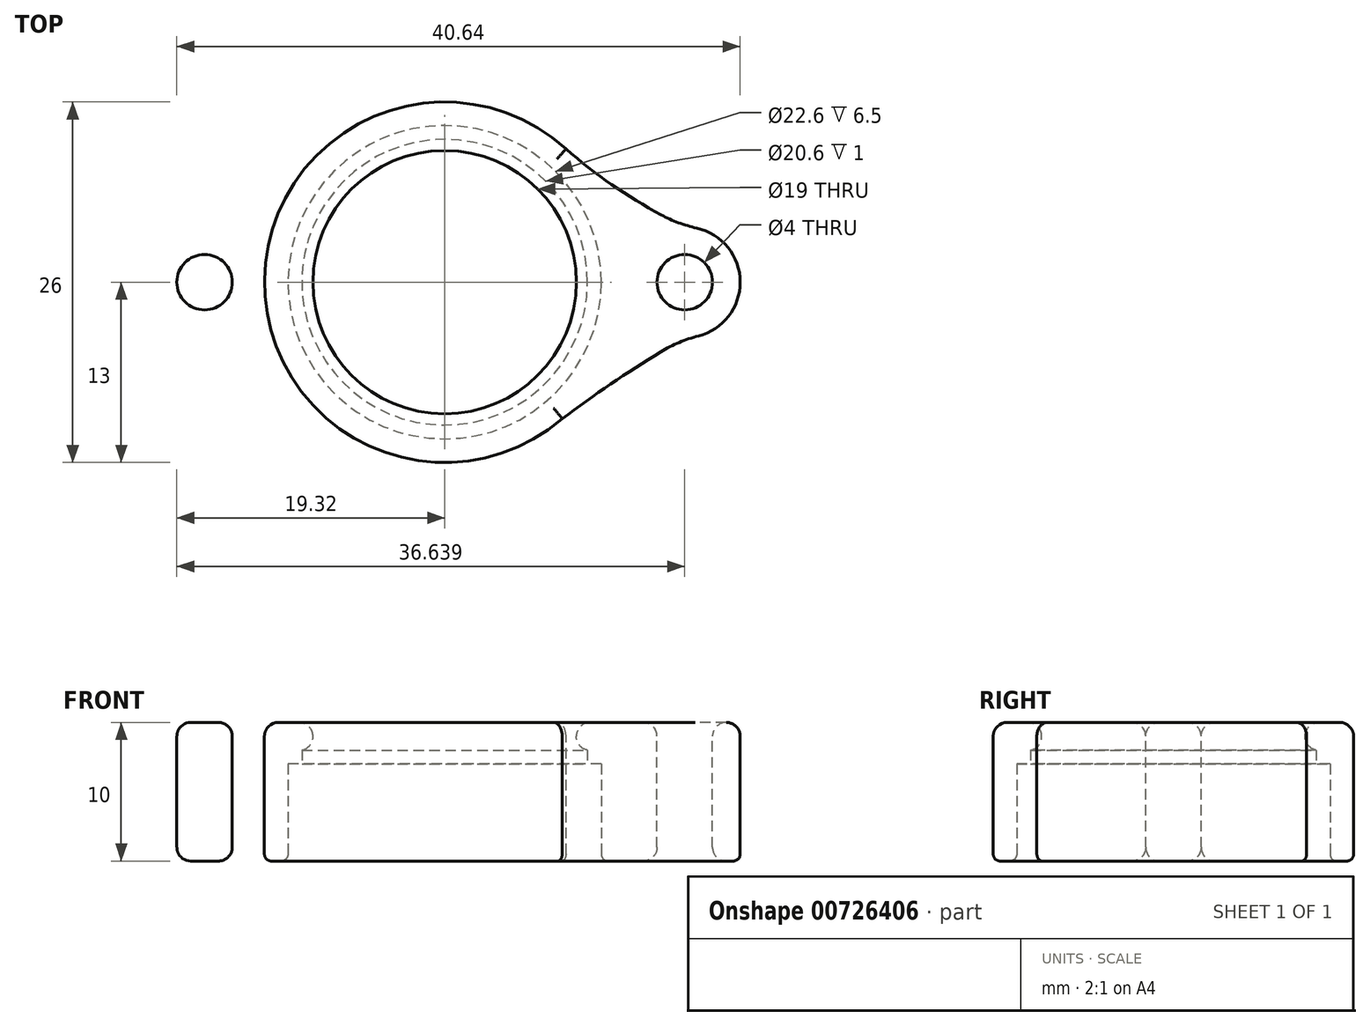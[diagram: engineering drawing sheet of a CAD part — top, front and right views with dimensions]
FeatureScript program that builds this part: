
annotation { "Feature Type Name" : "Feature", "Feature Type Description" : "" }
export const myFeature = defineFeature(function(context is Context, id is Id, definition is map)
    precondition{}
    {
        {
            var Q0;
            Q0=qCreatedBy(makeId("Top.planeOp"),FACE);
            var sketch = newSketch(context, id + "F0", { "sketchPlane" : qUnion([Q0])});
            skCircle(sketch, "E0", {"center": v(0, 0) * mm, "radius": 11.3 * mm});
            skCircle(sketch, "E1", {"center": v(0, 0) * mm, "radius": 13 * mm});
            skSolve(sketch);
        }
        {
            var Q0;
            Q0=makeQuery(id+"F0.imprint","IMPRINT",FACE,{"disambiguationData":[TD([[makeQuery(id+"F0.imprint","IMPRINT",EDGE,{"derivedFrom":sQuery(id+"F0.wireOp",EDGE,"E0")}),-1.0]])]});
            extrude(context, id + "F1", {"entities" : qUnion([Q0]), "depth" : 7 * mm, "offsetDistance" : 25 * mm});
        }
        {
            var Q0;
            Q0=makeQuery(id+"F1.opExtrude","CAP_FACE",FACE,{"disambiguationData":[OSD([sQuery(id+"F0.wireOp",EDGE,"E0"),sQuery(id+"F0.wireOp",EDGE,"E1")])],"isStart":false});
            var sketch = newSketch(context, id + "F2", { "sketchPlane" : qUnion([Q0])});
            skCircle(sketch, "E2.0", {"center": v(0, 0) * mm, "radius": 15 * mm});
            skSolve(sketch);
        }
        {
            var Q0;
            Q0=makeQuery(id+"F2.imprint","IMPRINT",FACE,{"disambiguationData":[TD([[makeQuery(id+"F2.imprint","IMPRINT",EDGE,{"derivedFrom":makeQuery(id+"F1.opExtrude","CAP_EDGE",EDGE,{"disambiguationData":[OSD([sQuery(id+"F0.wireOp",EDGE,"E0")])],"isStart":false})}),1.0]])]});
            var Q1;
            Q1=makeQuery(id+"F2.imprint","IMPRINT",FACE,{"disambiguationData":[TD([[makeQuery(id+"F2.imprint","IMPRINT",EDGE,{"derivedFrom":makeQuery(id+"F1.opExtrude","CAP_EDGE",EDGE,{"disambiguationData":[OSD([sQuery(id+"F0.wireOp",EDGE,"E0")])],"isStart":false})}),-1.0]])]});
            extrude(context, id + "F3", {"entities" : qUnion([Q0, Q1]), "operationType" : NewBodyOperationType.ADD, "depth" : 3 * mm, "offsetDistance" : 25 * mm});
        }
        {
            var Q0;
            Q0=makeQuery(id+"F3.opExtrude","CAP_FACE",FACE,{"disambiguationData":[OSD([sQuery(id+"F0.wireOp",EDGE,"E1")])],"isStart":true});
            var sketch = newSketch(context, id + "F4", { "sketchPlane" : qUnion([Q0])});
            skCircle(sketch, "E3.0", {"center": v(0, 0) * mm, "radius": 10.3 * mm});
            skSolve(sketch);
        }
        {
            var Q0;
            Q0=makeQuery(id+"F4.imprint","IMPRINT",FACE,{"disambiguationData":[TD([[makeQuery(id+"F4.imprint","IMPRINT",EDGE,{"derivedFrom":sQuery(id+"F4.wireOp",EDGE,"E3.0")}),1.0]])]});
            extrude(context, id + "F5", {"entities" : qUnion([Q0]), "operationType" : NewBodyOperationType.REMOVE, "oppositeDirection" : true, "depth" : 1 * mm, "offsetDistance" : 25 * mm});
        }
        {
            var Q0;
            Q0=makeQuery(id+"F3.opExtrude","CAP_FACE",FACE,{"disambiguationData":[OSD([sQuery(id+"F0.wireOp",EDGE,"E1")])],"isStart":false});
            var sketch = newSketch(context, id + "F6", { "sketchPlane" : qUnion([Q0])});
            skCircle(sketch, "E4", {"center": v(0, 0) * mm, "radius": 9.5 * mm});
            skSolve(sketch);
        }
        {
            var Q0;
            Q0=makeQuery(id+"F6.imprint","IMPRINT",FACE,{"disambiguationData":[TD([[makeQuery(id+"F6.imprint","IMPRINT",EDGE,{"derivedFrom":sQuery(id+"F6.wireOp",EDGE,"E4")}),1.0]])]});
            extrude(context, id + "F7", {"entities" : qUnion([Q0]), "operationType" : NewBodyOperationType.REMOVE, "oppositeDirection" : true, "depth" : 25 * mm, "offsetDistance" : 25 * mm});
        }
        {
            var Q0;
            Q0=makeQuery(id+"F3.opExtrude","CAP_FACE",FACE,{"disambiguationData":[OSD([sQuery(id+"F0.wireOp",EDGE,"E1")])],"isStart":false});
            var sketch = newSketch(context, id + "F8", { "sketchPlane" : qUnion([Q0])});
            skCircle(sketch, "E5", {"center": v(17.32, 0) * mm, "radius": 2 * mm});
            skArc(sketch, "E6", {"start": v(17.32, -4) * mm, "mid": v(21.32, 0) * mm, "end": v(17.32, 4) * mm});
            skArc(sketch, "E7", {"start": v(17.32, -4) * mm, "mid": v(12.81, -6.8) * mm, "end": v(8.48, -9.85) * mm});
            skArc(sketch, "E8", {"start": v(8.48, 9.85) * mm, "mid": v(12.69, 6.6) * mm, "end": v(17.32, 4) * mm});
            skCircle(sketch, "E9.MirrorC", {"center": v(-17.32, 0) * mm, "radius": 2 * mm});
            skArc(sketch, "E10.MirrorCS", {"start": v(-17.32, -4) * mm, "mid": v(-21.32, 0) * mm, "end": v(-17.32, 4) * mm});
            skArc(sketch, "E11.MirrorCS", {"start": v(-17.32, -4) * mm, "mid": v(-12.81, -6.8) * mm, "end": v(-8.48, -9.85) * mm});
            skArc(sketch, "E12.MirrorCS", {"start": v(-8.48, 9.85) * mm, "mid": v(-12.69, 6.6) * mm, "end": v(-17.32, 4) * mm});
            skArc(sketch, "E13", {"start": v(-8.48, 9.85) * mm, "mid": v(-12.77, 0) * mm, "end": v(-8.48, -9.85) * mm});
            skArc(sketch, "E14", {"start": v(8.48, -9.85) * mm, "mid": v(12.64, 0) * mm, "end": v(8.48, 9.85) * mm});
            skSolve(sketch);
        }
        {
            var Q0;
            Q0=makeQuery(id+"F8.imprint","IMPRINT",FACE,{"disambiguationData":[TD([[makeQuery(id+"F8.imprint","IMPRINT",EDGE,{"derivedFrom":sQuery(id+"F8.wireOp",EDGE,"E9.MirrorC")}),1.0]])]});
            var Q1;
            Q1=makeQuery(id+"F8.imprint","IMPRINT",FACE,{"disambiguationData":[TD([[makeQuery(id+"F8.imprint","IMPRINT",EDGE,{"derivedFrom":sQuery(id+"F8.wireOp",EDGE,"E5")}),-1.0]])]});
            var Q2;
            Q2=makeQuery(id+"F1.opExtrude","CAP_FACE",FACE,{"disambiguationData":[OSD([sQuery(id+"F0.wireOp",EDGE,"E0"),sQuery(id+"F0.wireOp",EDGE,"E1")])],"isStart":true});
            extrude(context, id + "F9", {"entities" : qUnion([Q0, Q1]), "operationType" : NewBodyOperationType.ADD, "endBound" : BoundingType.UP_TO_SURFACE, "oppositeDirection" : true, "depth" : 4 * mm, "endBoundEntityFace" : qUnion([Q2]), "offsetDistance" : 25 * mm});
        }
        {
            var Q0;
            Q0=makeQuery(id+"F9.opExtrude","SWEPT_EDGE",EDGE,{"disambiguationData":[OSD([sQuery(id+"F8.wireOp",EDGE,"E10.MirrorCS"),sQuery(id+"F8.wireOp",EDGE,"E12.MirrorCS")])]});
            var Q1;
            Q1=makeQuery(id+"F9.opExtrude","SWEPT_EDGE",EDGE,{"disambiguationData":[OSD([sQuery(id+"F8.wireOp",EDGE,"E10.MirrorCS"),sQuery(id+"F8.wireOp",EDGE,"E11.MirrorCS")])]});
            var Q2;
            Q2=makeQuery(id+"F9.opExtrude","SWEPT_EDGE",EDGE,{"disambiguationData":[OSD([sQuery(id+"F8.wireOp",EDGE,"E6"),sQuery(id+"F8.wireOp",EDGE,"E8")])]});
            var Q3;
            Q3=makeQuery(id+"F9.opExtrude","SWEPT_EDGE",EDGE,{"disambiguationData":[OSD([sQuery(id+"F8.wireOp",EDGE,"E6"),sQuery(id+"F8.wireOp",EDGE,"E7")])]});
            fillet(context, id + "F10", {"entities" : qUnion([Q0, Q1, Q2, Q3]), "radius" : 10 * mm, "tangentPropagation" : true, "allowEdgeOverflow" : false});
        }
        {
            var Q0;
            Q0=makeQuery(id+"F7.boolean.opBoolean","COPY",EDGE,{"derivedFrom":makeQuery(id+"F7.opExtrude","CAP_EDGE",EDGE,{"disambiguationData":[OSD([sQuery(id+"F6.wireOp",EDGE,"E4")])],"isStart":true})});
            var Q1;
            Q1=makeQuery(id+"F7.boolean.opBoolean","INTERSECT",EDGE,{"derivedFrom":[makeQuery(id+"F5.boolean.opBoolean","COPY",FACE,{"derivedFrom":makeQuery(id+"F5.opExtrude","CAP_FACE",FACE,{"disambiguationData":[OSD([sQuery(id+"F4.wireOp",EDGE,"E3.0")])],"isStart":false})}),makeQuery(id+"F7.opExtrude","SWEPT_FACE",FACE,{"disambiguationData":[OSD([sQuery(id+"F6.wireOp",EDGE,"E4")])]})]});
            fillet(context, id + "F11", {"entities" : qUnion([Q0, Q1]), "radius" : 1 * mm, "tangentPropagation" : true, "allowEdgeOverflow" : false});
        }
        {
            var Q0;
            Q0=makeQuery(id+"F9.opExtrude","CAP_EDGE",EDGE,{"disambiguationData":[OSD([sQuery(id+"F8.wireOp",EDGE,"E9.MirrorC")])],"isStart":true});
            var Q1;
            Q1=makeQuery(id+"F9.opExtrude","CAP_EDGE",EDGE,{"disambiguationData":[OSD([sQuery(id+"F8.wireOp",EDGE,"E5")])],"isStart":true});
            var Q2;
            Q2=makeQuery(id+"F9.opExtrude","CAP_EDGE",EDGE,{"disambiguationData":[OSD([sQuery(id+"F8.wireOp",EDGE,"E5")])],"isStart":false});
            var Q3;
            Q3=makeQuery(id+"F9.opExtrude","CAP_EDGE",EDGE,{"disambiguationData":[OSD([sQuery(id+"F8.wireOp",EDGE,"E9.MirrorC")])],"isStart":false});
            fillet(context, id + "F12", {"entities" : qUnion([Q0, Q1, Q2, Q3]), "radius" : 1 * mm, "tangentPropagation" : true, "allowEdgeOverflow" : false});
        }
        {
            var Q0;
            Q0=makeQuery(id+"F1.opExtrude","CAP_EDGE",EDGE,{"disambiguationData":[OSD([sQuery(id+"F0.wireOp",EDGE,"E0")])],"isStart":true});
            var Q1;
            Q1=makeQuery(id+"F9.opExtrude","CAP_EDGE",EDGE,{"disambiguationData":[OSD([sQuery(id+"F8.wireOp",EDGE,"E11.MirrorCS")])],"isStart":false});
            var Q2;
            {var subQ0=sQuery(id+"F8.wireOp",EDGE,"E7");var subQ1=sQuery(id+"F0.wireOp",EDGE,"E1");Q2=makeQuery(id+"F9.boolean.opBoolean","SPLIT",EDGE,{"disambiguationData":[TD([makeQuery(id+"F9.opExtrude","SWEPT_FACE",FACE,{"disambiguationData":[OSD([subQ0])]})])],"derivedFrom":makeQuery(id+"F1.opExtrude","CAP_EDGE",EDGE,{"disambiguationData":[OSD([subQ1])],"isStart":true})});}
            var Q3;
            Q3=makeQuery(id+"F9.opExtrude","CAP_EDGE",EDGE,{"disambiguationData":[OSD([sQuery(id+"F8.wireOp",EDGE,"E7")])],"isStart":false});
            var Q4;
            {var subQ0=sQuery(id+"F8.wireOp",EDGE,"E8");var subQ1=sQuery(id+"F0.wireOp",EDGE,"E1");Q4=makeQuery(id+"F9.boolean.opBoolean","SPLIT",EDGE,{"disambiguationData":[TD([makeQuery(id+"F9.opExtrude","SWEPT_FACE",FACE,{"disambiguationData":[OSD([subQ0])]})])],"derivedFrom":makeQuery(id+"F1.opExtrude","CAP_EDGE",EDGE,{"disambiguationData":[OSD([subQ1])],"isStart":true})});}
            fillet(context, id + "F13", {"entities" : qUnion([Q0, Q1, Q2, Q3, Q4]), "radius" : 0.5 * mm, "tangentPropagation" : true, "allowEdgeOverflow" : false});
        }
        {
            var Q0;
            {var subQ0=sQuery(id+"F0.wireOp",EDGE,"E1");Q0=makeQuery(id+"F9.boolean.opBoolean","MERGE",FACE,{"derivedFrom":[makeQuery(id+"F3.opExtrude","CAP_FACE",FACE,{"disambiguationData":[OSD([subQ0])],"isStart":false}),makeQuery(id+"F9.opExtrude","CAP_FACE",FACE,{"disambiguationData":[OSD([subQ0,sQuery(id+"F8.wireOp",EDGE,"E5"),sQuery(id+"F8.wireOp",EDGE,"E6"),sQuery(id+"F8.wireOp",EDGE,"E7"),sQuery(id+"F8.wireOp",EDGE,"E8")])],"isStart":true}),makeQuery(id+"F9.opExtrude","CAP_FACE",FACE,{"disambiguationData":[OSD([subQ0,sQuery(id+"F8.wireOp",EDGE,"E9.MirrorC"),sQuery(id+"F8.wireOp",EDGE,"E10.MirrorCS"),sQuery(id+"F8.wireOp",EDGE,"E11.MirrorCS"),sQuery(id+"F8.wireOp",EDGE,"E12.MirrorCS")])],"isStart":true})]});}
            fillet(context, id + "F14", {"entities" : qUnion([Q0]), "radius" : 1 * mm, "tangentPropagation" : true, "allowEdgeOverflow" : false});
        }
    });
